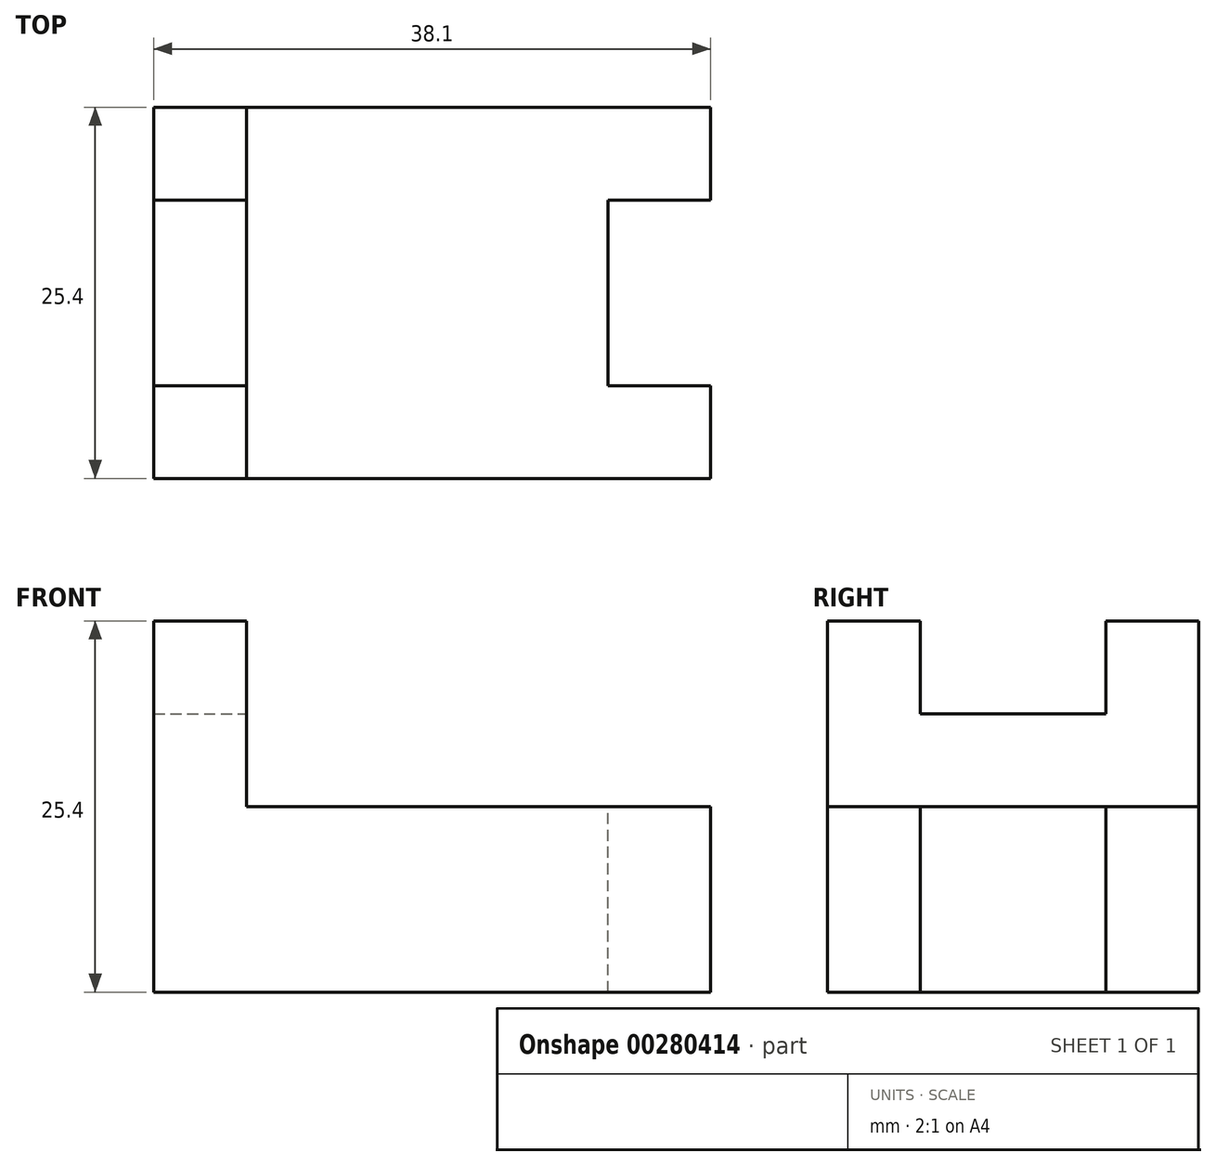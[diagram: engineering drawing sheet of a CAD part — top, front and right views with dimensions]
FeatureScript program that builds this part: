
annotation { "Feature Type Name" : "Feature", "Feature Type Description" : "" }
export const myFeature = defineFeature(function(context is Context, id is Id, definition is map)
    precondition{}
    {
        {
            var Q0;
            Q0=qCreatedBy(makeId("Front.planeOp"),FACE);
            var sketch = newSketch(context, id + "F0", { "sketchPlane" : qUnion([Q0])});
            skLineSegment(sketch, "E0", {"start": v(0, 25.4) * mm, "end": v(0, 0) * mm});
            skLineSegment(sketch, "E1", {"start": v(0, 0) * mm, "end": v(38.1, 0) * mm});
            skLineSegment(sketch, "E2", {"start": v(38.1, 0) * mm, "end": v(38.1, 12.7) * mm});
            skLineSegment(sketch, "E3", {"start": v(38.1, 12.7) * mm, "end": v(6.35, 12.7) * mm});
            skLineSegment(sketch, "E4", {"start": v(6.35, 12.7) * mm, "end": v(6.35, 25.4) * mm});
            skLineSegment(sketch, "E5", {"start": v(6.35, 25.4) * mm, "end": v(0, 25.4) * mm});
            skSolve(sketch);
        }
        {
            var Q0;
            Q0 = qSketchRegion(id + "FbR0VJo8r4ktwRy_1", true);
            var Q1;
            Q1 = qSketchRegion(id + "F0", true);
            extrude(context, id + "F1", {"entities" : qUnion([Q0, Q1]), "depth" : 25.4 * mm});
        }
        {
            var Q0;
            Q0=makeQuery(id+"F1.opExtrude","SWEPT_FACE",FACE,{"disambiguationData":[OSD([sQuery(id+"F0.wireOp",EDGE,"E5")])]});
            var sketch = newSketch(context, id + "F2", { "sketchPlane" : qUnion([Q0])});
            skLineSegment(sketch, "E6.bottom", {"start": v(0, -6.35) * mm, "end": v(6.35, -6.35) * mm});
            skLineSegment(sketch, "E6.top", {"start": v(0, -19.05) * mm, "end": v(6.35, -19.05) * mm});
            skLineSegment(sketch, "E6.left", {"start": v(0, -6.35) * mm, "end": v(0, -19.05) * mm});
            skLineSegment(sketch, "E6.right", {"start": v(6.35, -6.35) * mm, "end": v(6.35, -19.05) * mm});
            skSolve(sketch);
        }
        {
            var Q0;
            Q0 = qSketchRegion(id + "F2", true);
            extrude(context, id + "F3", {"entities" : qUnion([Q0]), "operationType" : NewBodyOperationType.REMOVE, "oppositeDirection" : true, "depth" : 6.35 * mm});
        }
        {
            var Q0;
            Q0=makeQuery(id+"F1.opExtrude","SWEPT_FACE",FACE,{"disambiguationData":[OSD([sQuery(id+"F0.wireOp",EDGE,"E3")])]});
            var sketch = newSketch(context, id + "F4", { "sketchPlane" : qUnion([Q0])});
            skLineSegment(sketch, "E7.bottom", {"start": v(38.1, -6.35) * mm, "end": v(31.09, -6.35) * mm});
            skLineSegment(sketch, "E7.top", {"start": v(38.1, -19.05) * mm, "end": v(31.09, -19.05) * mm});
            skLineSegment(sketch, "E7.left", {"start": v(38.1, -6.35) * mm, "end": v(38.1, -19.05) * mm});
            skLineSegment(sketch, "E7.right", {"start": v(31.09, -6.35) * mm, "end": v(31.09, -19.05) * mm});
            skSolve(sketch);
        }
        {
            var Q0;
            Q0 = qSketchRegion(id + "F4", true);
            extrude(context, id + "F5", {"entities" : qUnion([Q0]), "operationType" : NewBodyOperationType.REMOVE, "oppositeDirection" : true, "depth" : 12.7 * mm});
        }
    });
